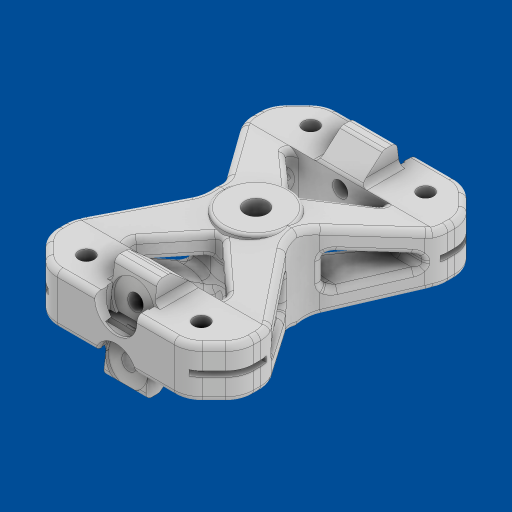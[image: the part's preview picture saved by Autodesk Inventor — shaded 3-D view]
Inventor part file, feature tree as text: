
AUTODESK INVENTOR PART (.ipt)
format: ipt  version: 2023 (Build 270158000, 158)  size: 1,785,344 bytes
history: native  units: mm
features: extrude x18, fillet x16, sketch x6, chamfer x6, plane x1, loft x1, mirror x1, other x1
ambient origin geometry x8: Origin, YZ Plane, XZ Plane, XY Plane, X Axis, Y Axis, Z Axis, Center Point
bodies: Body1 (feature_tree)
feature tree (50):
  sketch  "Sketch1"  dims[d13=261.822mm d14=7.45mm]
  plane  "Work Plane1"
  sketch  "Sketch2"  dims[d15=27.223mm d17=1.0mm]
  extrude  "Extrusion26"  Depth=7.45mm
  extrude  "Extrusion27"  Depth=1.0mm
  extrude  "Extrusion28"  Depth=100.0mm
  loft  "Loft4"
  extrude  "Extrusion30"  Depth=1.0mm
  extrude  "Extrusion31"  Depth=2.0mm
  extrude  "Extrusion32"  Depth=2.0mm
  extrude  "Extrusion33"  Depth=2.0mm
  sketch  "Sketch13"  dims[d23=2.0mm d25=1.0mm]
  extrude  "Extrusion34"  Depth=2.0mm
  extrude  "Extrusion35"  Depth=2.0mm
  extrude  "Extrusion36"  Depth=10.0mm TaperAngle=0.0deg
  extrude  "Extrusion37"  Depth=2.0mm
  fillet  "Fillet8"  Radius=24.0mm
  extrude  "Extrusion38"  Depth=2.0mm TaperAngle=0.0deg
  chamfer  "Chamfer7"  Distance=8.0mm
  chamfer  "Chamfer8"  Distance=19.96mm
  fillet  "Fillet9"  Radius=15.0mm
  mirror  "Mirror1"
  extrude  "Extrusion39"  TaperAngle=0.0deg  [1 undecoded]
  extrude  "Extrusion40"  TaperAngle=0.0deg  [1 undecoded]
  fillet  "Fillet10"  Radius=2.0mm
  fillet  "Fillet11"  Radius=2.0mm
  extrude  "Extrusion41"  Depth=2.0mm TaperAngle=0.0deg
  sketch  "Sketch15"  dims[d28=90.0deg d29=5.5mm d30=15.0mm d31=65.0mm d56=12.0mm d74=1.0mm d75=8.0mm d148=244.423mm d149=41.005864mm d150=244.423mm d151=5.5mm d152=5.5mm d153=5.5mm d154=15.0mm d155=15.0mm d156=18.0mm d157=5.5mm d158=160.0mm d159=10.0mm d160=0.0mm d161=8.0mm d162=24.0mm d163=30.0mm d164=0.0mm d165=8.0mm d166=0.0mm d167=19.96mm d168=15.0mm d169=0.0mm d170=0.0mm d171=90.0deg d172=0.0mm d173=90.0deg d178=2.0mm d179=0.0mm d180=2.0mm d181=15.0mm d182=0.0mm d183=15.0mm d184=0.0mm d185=15.0mm d186=0.0mm d187=15.0mm d188=15.0mm d189=15.0mm d190=2.5mm d191=15.0mm d192=15.0mm d193=5.5mm d194=5.5mm d195=1.0mm d196=0.0mm d197=16.0mm d198=0.0mm d199=15.0mm d200=0.0mm d201=15.0mm d202=0.0mm d203=2.0mm d204=1.0mm d205=0.0mm d206=10.0mm d207=10.0mm d208=45.0deg d209=10.0mm d210=10.0mm d211=45.0deg d212=10.0mm d213=15.0mm d214=0.0mm d215=15.0mm d216=15.0mm d217=0.0mm d218=10.0mm d219=10.0mm d220=30.0mm d221=0.0mm d226=8.0mm d227=7.0mm d228=45.0deg d229=7.0mm d230=8.0mm d231=45.0deg d232=12.0mm d233=9.0mm d234=45.0deg d235=9.0mm d236=12.0mm d237=45.0deg d238=2.0mm d239=2.0mm d240=2.0mm d241=1.0mm d242=2.0mm d244=7.5mm d245=7.5mm d246=90.0deg d247=16.0mm d248=70.0mm d249=0.0mm d256=15.0mm d257=30.0mm d258=0.0mm d259=20.0mm d260=0.0mm d261=20.0mm d262=5.0mm d263=2.0mm d264=2.0mm d266=2.0mm d267=2.0mm d268=2.0mm d76=0.5mm d77=0.872665mm d144=0.5mm d145=0.872665mm d146=0.5mm d147=0.872665mm d243=0.0mm d269=0.0mm d270=0.0mm d271=0.0mm]
  chamfer  "Chamfer9"  Distance=15.0mm
  chamfer  "Chamfer10"  Distance=15.0mm
  chamfer  "Chamfer11"  Distance=15.0mm
  chamfer  "Chamfer12"  Distance=15.0mm
  fillet  "Fillet12"  Radius=15.0mm
  fillet  "Fillet13"  Radius=2.5mm
  fillet  "Fillet14"  Radius=15.0mm
  fillet  "Fillet15"  Radius=15.0mm
  fillet  "Fillet16"  Radius=5.5mm
  extrude  "Extrusion43"  Depth=2.0mm
  extrude  "Extrusion45"  Depth=2.0mm TaperAngle=0.0deg
  extrude  "Extrusion46"  Depth=2.0mm TaperAngle=0.0deg
  fillet  "Fillet17"  Radius=15.0mm
  fillet  "Fillet18"  Radius=15.0mm
  fillet  "Fillet19"  Radius=2.0mm
  fillet  "Fillet20"  Radius=1.0mm
  fillet  "Fillet22"  Radius=10.0mm
  fillet  "Fillet23"  Radius=10.0mm
  fillet  "Fillet24"  Radius=10.0mm
  sketch  "Sketch12"  dims[d21=35.0mm d22=100.0mm]
  other  "Edges5"
  sketch  "Sketch14"  dims[d26=90.0deg d27=1.0mm]
note: 2 required parameter values undecoded (feature->parameter linkage not recoverable at this tier; creation-order binding heuristic only, values carry confidence <= 0.55)
